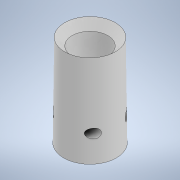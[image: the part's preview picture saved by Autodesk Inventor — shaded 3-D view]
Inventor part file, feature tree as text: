
AUTODESK INVENTOR PART (.ipt)
format: ipt  version: 2020 (Build 240168000, 168)  size: 180,224 bytes
history: native  units: in
note: dims shown in document units (in); Inventor stores cm internally (conversion verified against a paired STEP export)
features: sketch x3, hole x2, revolve x1, mirror x1
ambient origin geometry x8: Origin, YZ Plane, XZ Plane, XY Plane, X Axis, Y Axis, Z Axis, Center Point
bodies: Solid1 (feature_tree)
feature tree (7):
  revolve  "Revolution1"  [1 undecoded]
  hole  "Hole2"  [1 undecoded]
  hole  "Hole3"  [1 undecoded]
  mirror  "Mirror1"
  sketch  "Sketch1"  dims[d0=0.245in d1=0.0in]
  sketch  "Sketch3"  dims[d2=1.5in d3=90.0deg]
  sketch  "Sketch4"  dims[d4=0.03in d5=0.325in d6=165.0deg d7=0.5in d8=90.0deg d18=45.0deg d19=0.211in d20=0.25in d21=0.375in d22=0.25in d23=0.5635in d24=0.25in d25=0.0in d28=0.188in d29=0.5in d30=0.188in d31=0.5in d32=90.0deg d33=0.177in d34=0.328in d35=0.119in d36=0.25in d37=0.5635in d38=0.484in d39=0.0in d47=0.3779in d58=0.3388in]
note: 3 required parameter values undecoded (feature->parameter linkage not recoverable at this tier; creation-order binding heuristic only, values carry confidence <= 0.55)